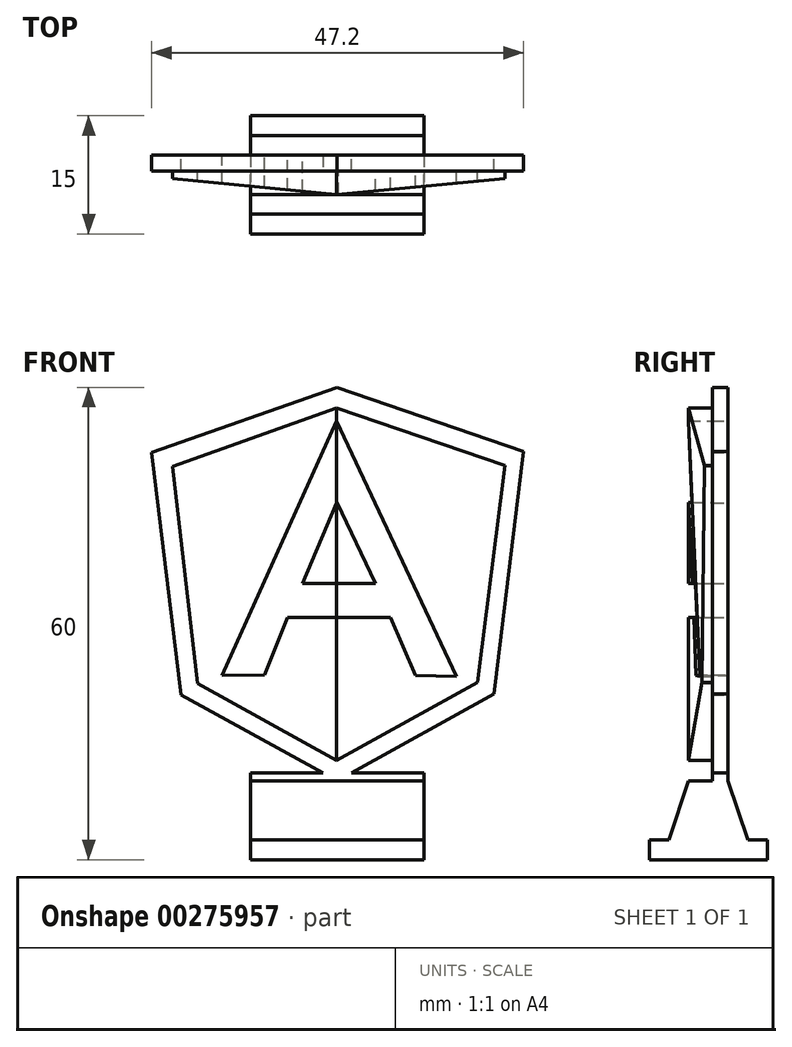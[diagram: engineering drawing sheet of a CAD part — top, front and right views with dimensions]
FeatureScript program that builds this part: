
annotation { "Feature Type Name" : "Feature", "Feature Type Description" : "" }
export const myFeature = defineFeature(function(context is Context, id is Id, definition is map)
    precondition{}
    {
        {
            var Q0;
            Q0=qCreatedBy(makeId("Front.planeOp"),FACE);
            var sketch = newSketch(context, id + "F0", { "sketchPlane" : qUnion([Q0])});
            skLineSegment(sketch, "E0", {"start": v(-0.08, 25) * mm, "end": v(-23.6, 16.72) * mm});
            skLineSegment(sketch, "E1", {"start": v(-23.6, 16.72) * mm, "end": v(-19.88, -14.1) * mm});
            skLineSegment(sketch, "E2", {"start": v(-19.88, -14.1) * mm, "end": v(-0.05, -25) * mm});
            skLineSegment(sketch, "E3", {"start": v(-0.05, -25) * mm, "end": v(19.88, -13.95) * mm});
            skLineSegment(sketch, "E4", {"start": v(19.88, -13.95) * mm, "end": v(23.6, 16.87) * mm});
            skLineSegment(sketch, "E5", {"start": v(23.6, 16.87) * mm, "end": v(-0.08, 25) * mm});
            skLineSegment(sketch, "E6", {"start": v(21.25, 15.09) * mm, "end": v(-0.13, 22.38) * mm});
            skLineSegment(sketch, "E7", {"start": v(-0.13, 22.38) * mm, "end": v(-0.13, -22.4) * mm});
            skLineSegment(sketch, "E8", {"start": v(-0.13, -22.4) * mm, "end": v(17.8, -12.48) * mm});
            skLineSegment(sketch, "E9", {"start": v(17.8, -12.48) * mm, "end": v(21.25, 15.09) * mm});
            skLineSegment(sketch, "E10", {"start": v(-20.96, 14.95) * mm, "end": v(-17.77, -12.6) * mm});
            skLineSegment(sketch, "E11", {"start": v(-17.77, -12.6) * mm, "end": v(-0.13, -22.4) * mm});
            skLineSegment(sketch, "E12", {"start": v(-0.13, -22.4) * mm, "end": v(-0.13, 22.38) * mm});
            skLineSegment(sketch, "E13", {"start": v(-0.13, 22.38) * mm, "end": v(-20.96, 14.95) * mm});
            skLineSegment(sketch, "E14", {"start": v(-0.12, -4.2) * mm, "end": v(-0.13, -4.2) * mm});
            skLineSegment(sketch, "E15", {"start": v(-0.13, -4.2) * mm, "end": v(-6.33, -4.2) * mm});
            skLineSegment(sketch, "E16", {"start": v(-6.33, -4.2) * mm, "end": v(-9.25, -11.5) * mm});
            skLineSegment(sketch, "E17", {"start": v(-9.25, -11.5) * mm, "end": v(-14.68, -11.6) * mm});
            skLineSegment(sketch, "E18", {"start": v(-14.68, -11.6) * mm, "end": v(-0.13, 20.75) * mm});
            skLineSegment(sketch, "E19", {"start": v(-0.13, 20.75) * mm, "end": v(-0.13, 20.75) * mm});
            skLineSegment(sketch, "E20", {"start": v(5.19, -0.07) * mm, "end": v(-0.1, 10.38) * mm});
            skLineSegment(sketch, "E21", {"start": v(-0.1, 10.38) * mm, "end": v(-4.42, 0.1) * mm});
            skLineSegment(sketch, "E22", {"start": v(-4.42, 0.1) * mm, "end": v(-0.13, 0.1) * mm});
            skLineSegment(sketch, "E23", {"start": v(-0.13, 0.1) * mm, "end": v(5.19, -0.07) * mm});
            skLineSegment(sketch, "E24", {"start": v(-0.13, 20.75) * mm, "end": v(-0.1, 10.38) * mm});
            skLineSegment(sketch, "E25", {"start": v(-0.1, 10.38) * mm, "end": v(4.82, 0.1) * mm});
            skLineSegment(sketch, "E26", {"start": v(4.82, 0.1) * mm, "end": v(-0.12, 0.1) * mm});
            skLineSegment(sketch, "E27", {"start": v(-0.12, 0.1) * mm, "end": v(-0.13, -4.2) * mm});
            skLineSegment(sketch, "E28", {"start": v(-0.13, -4.2) * mm, "end": v(6.7, -4.2) * mm});
            skLineSegment(sketch, "E29", {"start": v(6.7, -4.2) * mm, "end": v(9.9, -11.6) * mm});
            skLineSegment(sketch, "E30", {"start": v(9.9, -11.6) * mm, "end": v(15.08, -11.7) * mm});
            skLineSegment(sketch, "E31", {"start": v(15.08, -11.7) * mm, "end": v(-0.13, 20.75) * mm});
            skLineSegment(sketch, "E32", {"start": v(-11.05, -25) * mm, "end": v(10.95, -25) * mm});
            skSolve(sketch);
        }
        {
            var Q0;
            {var subQ3=sQuery(id+"F0.wireOp",EDGE,"E21");var subQ6=sQuery(id+"F0.wireOp",EDGE,"E7");var subQ9=makeQuery(id+"F0.imprint","INTERSECT",VERTEX,{"derivedFrom":[subQ6,subQ3]});Q0=makeQuery(id+"F0.imprint","IMPRINT",FACE,{"disambiguationData":[TD([[makeQuery(id+"F0.imprint","IMPRINT",EDGE,{"disambiguationData":[TD([[subQ9,-1.0]])],"derivedFrom":subQ6}),1.0]])]});}
            var Q1;
            {var subQ0=sQuery(id+"F0.wireOp",EDGE,"E22");Q1=makeQuery(id+"F0.imprint","IMPRINT",FACE,{"disambiguationData":[TD([[makeQuery(id+"F0.imprint","IMPRINT",EDGE,{"derivedFrom":subQ0}),1.0]])]});}
            var Q2;
            Q2=makeQuery(id+"F0.imprint","IMPRINT",FACE,{"disambiguationData":[TD([[makeQuery(id+"F0.imprint","IMPRINT",EDGE,{"derivedFrom":sQuery(id+"F0.wireOp",EDGE,"E10")}),1.0]])]});
            var Q3;
            {var subQ2=sQuery(id+"F0.wireOp",EDGE,"E6");Q3=makeQuery(id+"F0.imprint","IMPRINT",FACE,{"disambiguationData":[TD([[makeQuery(id+"F0.imprint","IMPRINT",EDGE,{"derivedFrom":subQ2}),1.0]])]});}
            var Q4;
            Q4=makeQuery(id+"F0.imprint","IMPRINT",FACE,{"disambiguationData":[TD([[makeQuery(id+"F0.imprint","IMPRINT",EDGE,{"derivedFrom":sQuery(id+"F0.wireOp",EDGE,"E0")}),1.0]])]});
            var Q5;
            {var subQ1=sQuery(id+"F0.wireOp",EDGE,"E20");Q5=makeQuery(id+"F0.imprint","IMPRINT",FACE,{"disambiguationData":[TD([[makeQuery(id+"F0.imprint","IMPRINT",EDGE,{"derivedFrom":subQ1}),1.0]])]});}
            var Q6;
            {var subQ0=sQuery(id+"F0.wireOp",EDGE,"E23");var subQ1=sQuery(id+"F0.wireOp",EDGE,"E7");var subQ2=makeQuery(id+"F0.imprint","INTERSECT",VERTEX,{"derivedFrom":[subQ1,subQ0]});Q6=makeQuery(id+"F0.imprint","IMPRINT",FACE,{"disambiguationData":[TD([[makeQuery(id+"F0.imprint","IMPRINT",EDGE,{"disambiguationData":[TD([[subQ2,-1.0]])],"derivedFrom":subQ1}),-1.0]])]});}
            var Q7;
            {var subQ0=sQuery(id+"F0.wireOp",EDGE,"E24");var subQ1=sQuery(id+"F0.wireOp",EDGE,"E7");var subQ2=makeQuery(id+"F0.imprint","INTERSECT",VERTEX,{"derivedFrom":[subQ1,subQ0]});Q7=makeQuery(id+"F0.imprint","IMPRINT",FACE,{"disambiguationData":[TD([[makeQuery(id+"F0.imprint","IMPRINT",EDGE,{"disambiguationData":[TD([[subQ2,-1.0]])],"derivedFrom":subQ1}),1.0]])]});}
            var Q8;
            {var subQ0=sQuery(id+"F0.wireOp",EDGE,"E21");var subQ1=sQuery(id+"F0.wireOp",EDGE,"E7");var subQ2=makeQuery(id+"F0.imprint","INTERSECT",VERTEX,{"derivedFrom":[subQ1,subQ0]});Q8=makeQuery(id+"F0.imprint","IMPRINT",FACE,{"disambiguationData":[TD([[makeQuery(id+"F0.imprint","IMPRINT",EDGE,{"disambiguationData":[TD([[subQ2,-1.0]])],"derivedFrom":subQ1}),-1.0]])]});}
            var Q9;
            {var subQ0=sQuery(id+"F0.wireOp",EDGE,"E23");var subQ1=sQuery(id+"F0.wireOp",EDGE,"E7");var subQ2=makeQuery(id+"F0.imprint","INTERSECT",VERTEX,{"derivedFrom":[subQ1,subQ0]});Q9=makeQuery(id+"F0.imprint","IMPRINT",FACE,{"disambiguationData":[TD([[makeQuery(id+"F0.imprint","IMPRINT",EDGE,{"disambiguationData":[TD([[subQ2,-1.0]])],"derivedFrom":subQ1}),1.0]])]});}
            var Q10;
            {var subQ0=sQuery(id+"F0.wireOp",EDGE,"E24");var subQ1=sQuery(id+"F0.wireOp",EDGE,"E7");var subQ2=makeQuery(id+"F0.imprint","INTERSECT",VERTEX,{"derivedFrom":[subQ1,subQ0]});Q10=makeQuery(id+"F0.imprint","IMPRINT",FACE,{"disambiguationData":[TD([[makeQuery(id+"F0.imprint","IMPRINT",EDGE,{"disambiguationData":[TD([[subQ2,-1.0]])],"derivedFrom":subQ1}),-1.0]])]});}
            var Q11;
            {var subQ0=sQuery(id+"F0.wireOp",EDGE,"E27");var subQ1=sQuery(id+"F0.wireOp",EDGE,"E7");var subQ2=makeQuery(id+"F0.imprint","INTERSECT",VERTEX,{"derivedFrom":[subQ1,subQ0]});Q11=makeQuery(id+"F0.imprint","IMPRINT",FACE,{"disambiguationData":[TD([[makeQuery(id+"F0.imprint","IMPRINT",EDGE,{"disambiguationData":[TD([[subQ2,-1.0]])],"derivedFrom":subQ1}),-1.0]])]});}
            var Q12;
            {var subQ1=sQuery(id+"F0.wireOp",EDGE,"E7");var subQ3=sQuery(id+"F0.wireOp",EDGE,"E28");var subQ4=makeQuery(id+"F0.imprint","INTERSECT",VERTEX,{"derivedFrom":[subQ1,subQ3]});Q12=makeQuery(id+"F0.imprint","IMPRINT",FACE,{"disambiguationData":[TD([[makeQuery(id+"F0.imprint","IMPRINT",EDGE,{"disambiguationData":[TD([[subQ4,-1.0]])],"derivedFrom":subQ1}),-1.0]])]});}
            var Q13;
            {var subQ1=sQuery(id+"F0.wireOp",EDGE,"E7");var subQ3=sQuery(id+"F0.wireOp",EDGE,"E31");var subQ4=makeQuery(id+"F0.imprint","INTERSECT",VERTEX,{"derivedFrom":[subQ1,subQ3]});Q13=makeQuery(id+"F0.imprint","IMPRINT",FACE,{"disambiguationData":[TD([[makeQuery(id+"F0.imprint","IMPRINT",EDGE,{"disambiguationData":[TD([[subQ4,-1.0]])],"derivedFrom":subQ3}),-1.0]])]});}
            var Q14;
            {var subQ0=sQuery(id+"F0.wireOp",EDGE,"E19");Q14=makeQuery(id+"F0.imprint","IMPRINT",FACE,{"disambiguationData":[TD([[makeQuery(id+"F0.imprint","IMPRINT",EDGE,{"derivedFrom":subQ0}),-1.0]])]});}
            var Q15;
            {var subQ0=sQuery(id+"F0.wireOp",EDGE,"E14");Q15=makeQuery(id+"F0.imprint","IMPRINT",FACE,{"disambiguationData":[TD([[makeQuery(id+"F0.imprint","IMPRINT",EDGE,{"derivedFrom":subQ0}),-1.0]])]});}
            var Q16;
            {var subQ0=sQuery(id+"F0.wireOp",EDGE,"E31");var subQ1=sQuery(id+"F0.wireOp",EDGE,"E18");var subQ2=makeQuery(id+"F0.imprint","INTERSECT",VERTEX,{"derivedFrom":[subQ1,subQ0]});Q16=makeQuery(id+"F0.imprint","IMPRINT",FACE,{"disambiguationData":[TD([[makeQuery(id+"F0.imprint","IMPRINT",EDGE,{"disambiguationData":[TD([[subQ2,1.0]])],"derivedFrom":subQ1}),1.0]])]});}
            var Q17;
            {var subQ0=sQuery(id+"F0.wireOp",EDGE,"E31");var subQ1=sQuery(id+"F0.wireOp",EDGE,"E7");var subQ2=makeQuery(id+"F0.imprint","INTERSECT",VERTEX,{"derivedFrom":[subQ1,subQ0]});Q17=makeQuery(id+"F0.imprint","IMPRINT",FACE,{"disambiguationData":[TD([[makeQuery(id+"F0.imprint","IMPRINT",EDGE,{"disambiguationData":[TD([[subQ2,-1.0]])],"derivedFrom":subQ1}),-1.0]])]});}
            var Q18;
            {var subQ13=sQuery(id+"F0.wireOp",EDGE,"E20");Q18=makeQuery(id+"F0.imprint","IMPRINT",FACE,{"disambiguationData":[TD([[makeQuery(id+"F0.imprint","IMPRINT",EDGE,{"derivedFrom":subQ13}),-1.0]])]});}
            var Q19;
            {var subQ0=sQuery(id+"F0.wireOp",EDGE,"E16");Q19=makeQuery(id+"F0.imprint","IMPRINT",FACE,{"disambiguationData":[TD([[makeQuery(id+"F0.imprint","IMPRINT",EDGE,{"derivedFrom":subQ0}),-1.0]])]});}
            extrude(context, id + "F1", {"entities" : qUnion([Q0, Q1, Q2, Q3, Q4, Q5, Q6, Q7, Q8, Q9, Q10, Q11, Q12, Q13, Q14, Q15, Q16, Q17, Q18, Q19]), "depth" : 2 * mm});
        }
        {
            var Q0;
            Q0=makeQuery(id+"F0.imprint","IMPRINT",FACE,{"disambiguationData":[TD([[makeQuery(id+"F0.imprint","IMPRINT",EDGE,{"derivedFrom":sQuery(id+"F0.wireOp",EDGE,"E10")}),1.0]])]});
            var Q1;
            {var subQ2=sQuery(id+"F0.wireOp",EDGE,"E6");Q1=makeQuery(id+"F0.imprint","IMPRINT",FACE,{"disambiguationData":[TD([[makeQuery(id+"F0.imprint","IMPRINT",EDGE,{"derivedFrom":subQ2}),1.0]])]});}
            var Q2;
            {var subQ0=sQuery(id+"F0.wireOp",EDGE,"E22");Q2=makeQuery(id+"F0.imprint","IMPRINT",FACE,{"disambiguationData":[TD([[makeQuery(id+"F0.imprint","IMPRINT",EDGE,{"derivedFrom":subQ0}),1.0]])]});}
            var Q3;
            {var subQ3=sQuery(id+"F0.wireOp",EDGE,"E21");var subQ6=sQuery(id+"F0.wireOp",EDGE,"E7");var subQ9=makeQuery(id+"F0.imprint","INTERSECT",VERTEX,{"derivedFrom":[subQ6,subQ3]});Q3=makeQuery(id+"F0.imprint","IMPRINT",FACE,{"disambiguationData":[TD([[makeQuery(id+"F0.imprint","IMPRINT",EDGE,{"disambiguationData":[TD([[subQ9,-1.0]])],"derivedFrom":subQ6}),1.0]])]});}
            extrude(context, id + "F2", {"entities" : qUnion([Q0, Q1, Q2, Q3]), "operationType" : NewBodyOperationType.ADD, "depth" : 5 * mm});
        }
        {
            var Q0;
            Q0=qCreatedBy(makeId("Top.planeOp"),FACE);
            var sketch = newSketch(context, id + "F3", { "sketchPlane" : qUnion([Q0])});
            skLineSegment(sketch, "E33.bottom", {"start": v(-20.96, -5) * mm, "end": v(21.25, -5) * mm});
            skLineSegment(sketch, "E33.top", {"start": v(-20.96, -3) * mm, "end": v(21.25, -3) * mm});
            skLineSegment(sketch, "E33.left", {"start": v(-20.96, -5) * mm, "end": v(-20.96, -3) * mm});
            skLineSegment(sketch, "E33.right", {"start": v(21.25, -5) * mm, "end": v(21.25, -3) * mm});
            skLineSegment(sketch, "E34", {"start": v(-0.12, -5) * mm, "end": v(21.25, -3) * mm});
            skLineSegment(sketch, "E35", {"start": v(-0.12, -5) * mm, "end": v(-20.96, -3) * mm});
            skSolve(sketch);
        }
        {
            var Q0;
            {var subQ0=sQuery(id+"F3.wireOp",EDGE,"E33.left");Q0=makeQuery(id+"F3.imprint","IMPRINT",FACE,{"disambiguationData":[TD([[makeQuery(id+"F3.imprint","IMPRINT",EDGE,{"derivedFrom":subQ0}),-1.0]])]});}
            var Q1;
            {var subQ0=sQuery(id+"F3.wireOp",EDGE,"E33.right");Q1=makeQuery(id+"F3.imprint","IMPRINT",FACE,{"disambiguationData":[TD([[makeQuery(id+"F3.imprint","IMPRINT",EDGE,{"derivedFrom":subQ0}),1.0]])]});}
            extrude(context, id + "F4", {"entities" : qUnion([Q0, Q1]), "operationType" : NewBodyOperationType.REMOVE, "oppositeDirection" : true, "depth" : 60 * mm, "symmetric" : true});
        }
        {
            var Q0;
            Q0=sQuery(id+"F0.wireOp",EDGE,"E32");
            var Q1;
            Q1=sQuery(id+"F0.wireOp",VERTEX,"E32.end");
            cPlane(context, id + "F5", {"entities" : qUnion([Q0, Q1]), "cplaneType" : CPlaneType.LINE_POINT, "offset" : 25 * mm, "width" : 150 * mm, "height" : 150 * mm});
        }
        {
            var Q0;
            Q0=qCreatedBy(id+"F5.planeOp",FACE);
            var sketch = newSketch(context, id + "F6", { "sketchPlane" : qUnion([Q0])});
            skLineSegment(sketch, "E36.bottom", {"start": v(0, -24) * mm, "end": v(-2, -24) * mm});
            skLineSegment(sketch, "E36.top", {"start": v(0, -25) * mm, "end": v(-2, -25) * mm});
            skLineSegment(sketch, "E36.left", {"start": v(0, -24) * mm, "end": v(0, -25) * mm});
            skLineSegment(sketch, "E36.right", {"start": v(-2, -24) * mm, "end": v(-2, -25) * mm});
            skLineSegment(sketch, "E37", {"start": v(0, -25) * mm, "end": v(2.5, -32.5) * mm});
            skLineSegment(sketch, "E38", {"start": v(2.5, -32.5) * mm, "end": v(5, -32.5) * mm});
            skLineSegment(sketch, "E39", {"start": v(5, -32.5) * mm, "end": v(5, -35) * mm});
            skLineSegment(sketch, "E40", {"start": v(5, -35) * mm, "end": v(-10, -35) * mm});
            skLineSegment(sketch, "E41", {"start": v(-10, -35) * mm, "end": v(-10, -32.5) * mm});
            skLineSegment(sketch, "E42", {"start": v(-10, -32.5) * mm, "end": v(-7.5, -32.5) * mm});
            skLineSegment(sketch, "E43", {"start": v(-7.5, -32.5) * mm, "end": v(-5, -25) * mm});
            skLineSegment(sketch, "E44", {"start": v(-5, -25) * mm, "end": v(-2, -25) * mm});
            skLineSegment(sketch, "E45", {"start": v(-2.5, -25) * mm, "end": v(-2.5, -35) * mm});
            skSolve(sketch);
        }
        {
            var Q0;
            Q0 = qSketchRegion(id + "F6", true);
            extrude(context, id + "F7", {"entities" : qUnion([Q0]), "operationType" : NewBodyOperationType.ADD, "oppositeDirection" : true, "depth" : 22 * mm});
        }
    });
